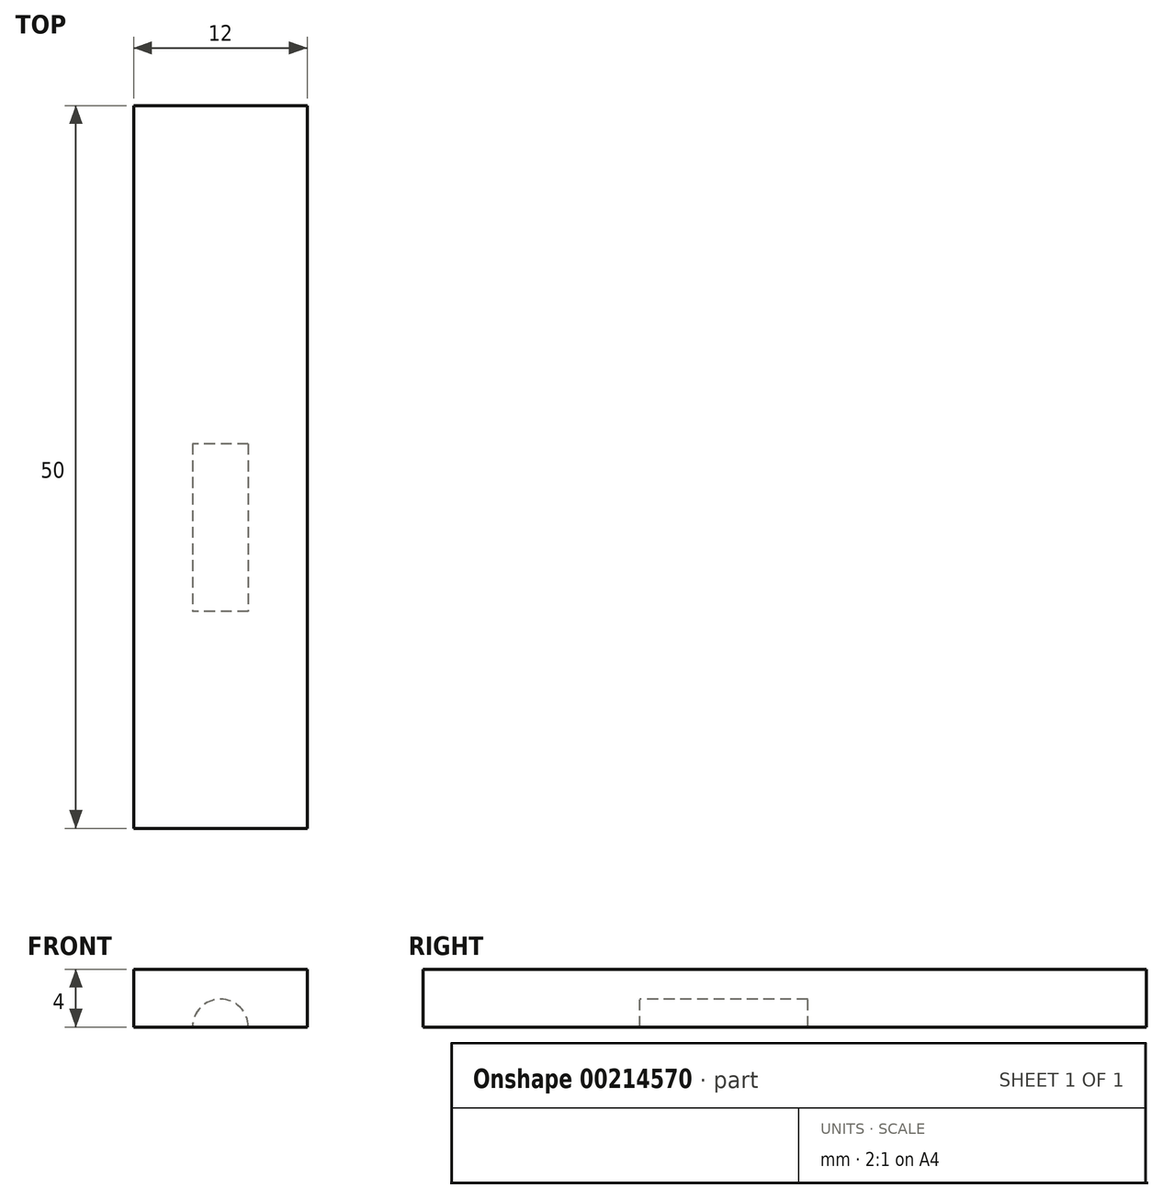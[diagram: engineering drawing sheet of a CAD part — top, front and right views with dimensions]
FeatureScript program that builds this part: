
annotation { "Feature Type Name" : "Feature", "Feature Type Description" : "" }
export const myFeature = defineFeature(function(context is Context, id is Id, definition is map)
    precondition{}
    {
        {
            var Q0;
            Q0=qCreatedBy(makeId("Top.planeOp"),FACE);
            var sketch = newSketch(context, id + "F0", { "sketchPlane" : qUnion([Q0])});
            skLineSegment(sketch, "E0.bottom", {"start": v(-6, 25) * mm, "end": v(6, 25) * mm});
            skLineSegment(sketch, "E0.top", {"start": v(-6, -25) * mm, "end": v(6, -25) * mm});
            skLineSegment(sketch, "E0.left", {"start": v(-6, 25) * mm, "end": v(-6, -25) * mm});
            skLineSegment(sketch, "E0.right", {"start": v(6, 25) * mm, "end": v(6, -25) * mm});
            skLineSegment(sketch, "E1", {"start": v(-6, -10) * mm, "end": v(6, -10) * mm, "construction": true});
            skPoint(sketch, "E2", {"position": v(-6, 0) * mm});
            skPoint(sketch, "E3", {"position": v(0, 25) * mm});
            skLineSegment(sketch, "E4", {"start": v(0, -10) * mm, "end": v(0, 1.6) * mm});
            skPoint(sketch, "E4.endSnap0", {"position": v(0, -10) * mm});
            skLineSegment(sketch, "E5", {"start": v(-1.92, 1.6) * mm, "end": v(1.92, 1.6) * mm});
            skPoint(sketch, "E6", {"position": v(0, 1.6) * mm});
            skLineSegment(sketch, "E7", {"start": v(-1.92, 1.6) * mm, "end": v(-1.93, -10) * mm});
            skLineSegment(sketch, "E8", {"start": v(1.92, 1.6) * mm, "end": v(1.93, -10) * mm});
            skLineSegment(sketch, "E9", {"start": v(-1.93, -10) * mm, "end": v(1.93, -10) * mm});
            skSolve(sketch);
        }
        {
            var Q0;
            Q0 = qSketchRegion(id + "F0", true);
            var Q1;
            Q1=makeQuery(id+"F0.imprint","IMPRINT",FACE,{"disambiguationData":[TD([[makeQuery(id+"F0.imprint","IMPRINT",EDGE,{"derivedFrom":sQuery(id+"F0.wireOp",EDGE,"E5")}),-1.0]])]});
            extrude(context, id + "F1", {"entities" : qUnion([Q0, Q1]), "depth" : 4 * mm});
        }
        {
            var Q0;
            {var subQ0=sQuery(id+"F0.wireOp",EDGE,"E4");Q0=makeQuery(id+"F0.imprint","IMPRINT",FACE,{"disambiguationData":[TD([[makeQuery(id+"F0.imprint","IMPRINT",EDGE,{"derivedFrom":subQ0}),1.0]])]});}
            var Q1;
            Q1=sQuery(id+"F0.wireOp",EDGE,"E4");
            revolve(context, id + "F2", {"operationType" : NewBodyOperationType.REMOVE, "entities" : qUnion([Q0]), "axis" : qUnion([Q1]), "revolveType" : RevolveType.ONE_DIRECTION, "angle" : 180 * degree});
        }
    });
